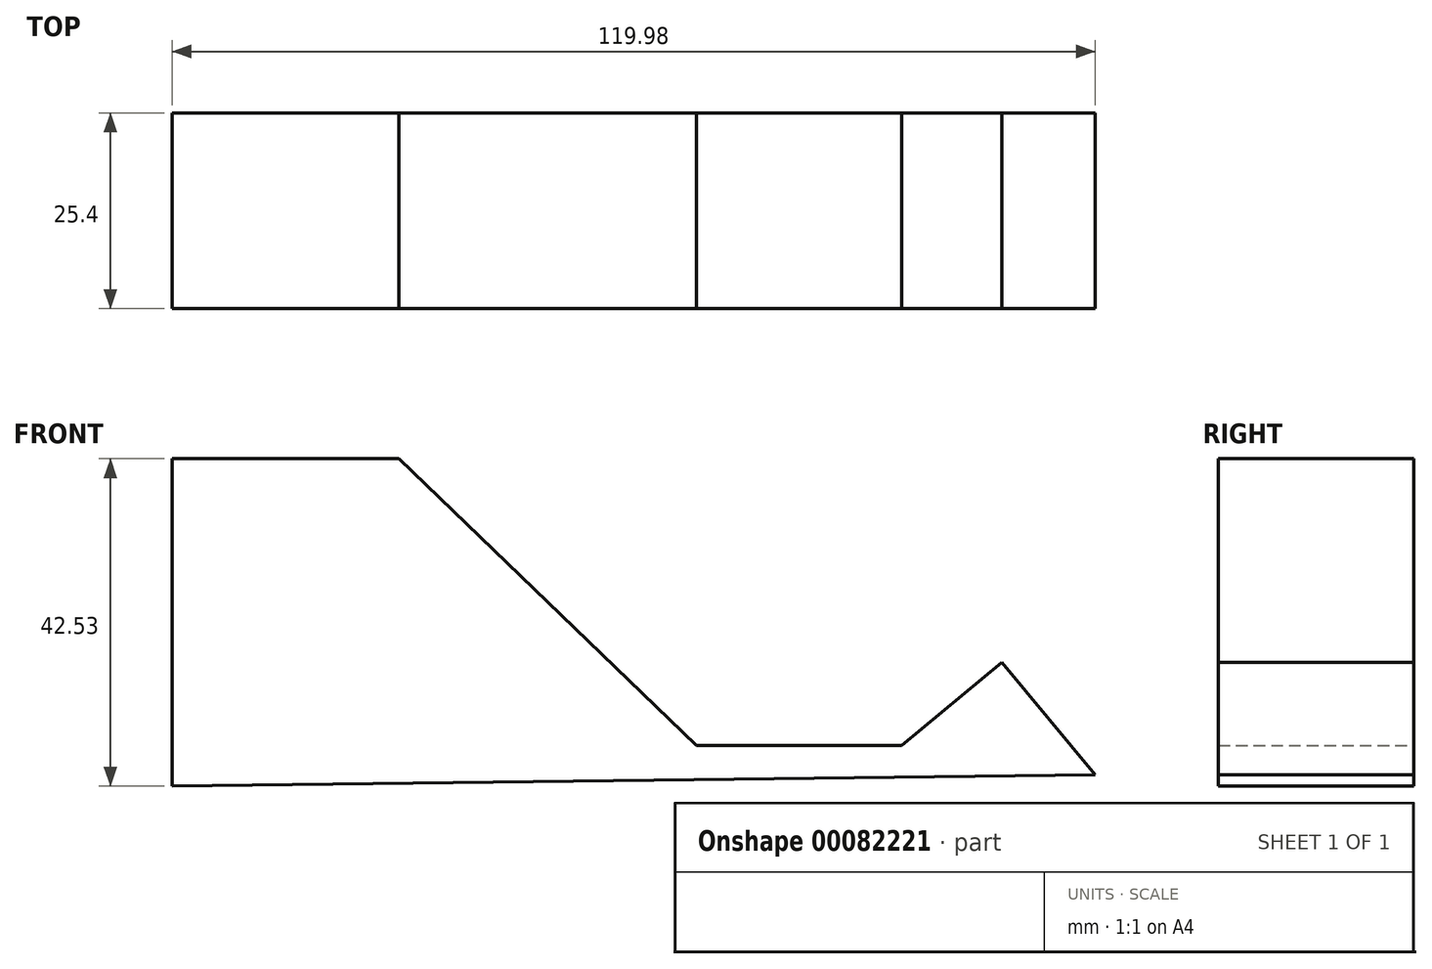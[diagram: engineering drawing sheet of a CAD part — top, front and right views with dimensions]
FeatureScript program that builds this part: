
annotation { "Feature Type Name" : "Feature", "Feature Type Description" : "" }
export const myFeature = defineFeature(function(context is Context, id is Id, definition is map)
    precondition{}
    {
        {
            var Q0;
            Q0=qCreatedBy(makeId("Front.planeOp"),FACE);
            var sketch = newSketch(context, id + "F0", { "sketchPlane" : qUnion([Q0])});
            skLineSegment(sketch, "E0", {"start": v(-59.42, -53.11) * mm, "end": v(-59.42, -10.58) * mm});
            skLineSegment(sketch, "E1", {"start": v(-59.42, -10.58) * mm, "end": v(-29.91, -10.58) * mm});
            skLineSegment(sketch, "E2", {"start": v(-29.91, -10.58) * mm, "end": v(8.75, -47.82) * mm});
            skLineSegment(sketch, "E3", {"start": v(8.75, -47.82) * mm, "end": v(35.4, -47.82) * mm});
            skLineSegment(sketch, "E4", {"start": v(35.4, -47.82) * mm, "end": v(48.43, -37.04) * mm});
            skLineSegment(sketch, "E5", {"start": v(48.43, -37.04) * mm, "end": v(60.56, -51.68) * mm});
            skLineSegment(sketch, "E6", {"start": v(60.56, -51.68) * mm, "end": v(-59.42, -53.11) * mm});
            skSolve(sketch);
        }
        {
            var Q0;
            Q0=makeQuery(id+"F0.imprint","IMPRINT",FACE,{"disambiguationData":[TD([[makeQuery(id+"F0.imprint","IMPRINT",EDGE,{"derivedFrom":sQuery(id+"F0.wireOp",EDGE,"E0")}),-1.0]])]});
            extrude(context, id + "F1", {"entities" : qUnion([Q0]), "depth" : 25.4 * mm});
        }
    });
